# Revit family: Genie_Site_ArticulatingBoom_(SX-180)a
name_source: partatom
category: Site
revit_build: Autodesk Revit 2018 (Build: 20190510_1515(x64)
units: mm (PartAtom-declared; Revit-internal decimal feet)

## family parameters
Always vertical = Yes
Cut with Voids When Loaded = No
OmniClass Number = 23.50.85.17.11
OmniClass Title = Electric and Battery Telescoping Platforms
Part Type = Normal
Round Connector Dimension = Use Diameter
Shared = No
Work Plane-Based = No

## types (1)
- SX-180
    Assembly Code = E1030900
    AssetType = Fixed
    BIMObjectName = Genie_Site_ArticulatingBoom_(SX-180)
    ClassificationName = Uniclass2015
    ClassificationValue = Pr_65_80_47_95
    Color = Grey & Blue
    Cost = 0 $
    Description = The highest reaching model in the line-up, the Genie® SX™-180 telescopic boom lift offers operators access to jobsites inaccessible by other booms, boom trucks and cranes. It is purpose-built to work on jobsites in the oil and gas industries and in industrial or commercial construction and in general maintenance applications.
    DocumentationLiterature = https://www.genielift.com
    DocumentationTechnical = https://www.genielift.com
    DurationUnit = Years
    ExpectedLife = 0
    Features = Genie XChassis™ system extends and retracts to provide stability on the job and a narrow profile for transport. 3.05 m (10 ft) rotating jib with 135˚ vertical and 60˚ horizontal articulation to easily position workers and gear. Standard 2.44 m (8 ft) self-levelling platform with an unrestricted capacity of 340 kg (750 lb). Drive-enable at full height for more productivity on the jobsite. Tackles the most extreme jobs with a working height of 56.9 m (186 ft) and horizontal reach of 24.4 m (80 ft).
    Finish = Painted Steel
    IfcExportAs = IfcTransportElement
    IfcExportType = IfcTransportElementType
    Keynote = X
    Manufacturer = Genie
    ManufacturerName = Genie
    Material = Painted Steel
    Model = Genie - Articulating Boom
    ModelNumber = SX-180
    ModelReference = Genie - Articulating Boom
    NBSDescription = Vertical lifting platforms
    NBSObjectName = Genie - Vertical lifting platforms
    NBSReference = 90-80-65/350
    NominalDepth = 2490 mm
    NominalHeight = 3050 mm  [stored 10.0066 ft]
    NominalLength = 16180 mm
    ProductionYear = 2019
    Size = 2.49m x 3.05m x 16.18m
    Type Comments = SX-180
    TypeName = Genie - Articulating Boom
    URL = http://www.genielift.co.uk
    WarrantyDurationLabor = 0
    WarrantyDurationParts = 0
    WarrantyDurationUnit = Years
    WarrantyGuarantorLabor = http://www.genielift.co.uk
    WarrantyGuarantorParts = http://www.genielift.co.uk
    _BSBibleVersion = 15
    _BimSpecGuid = 0
    _CurrentRevision = 1
    _DistributedBy = www.bimstore.co.uk

note: [stored X ft] marks values corroborated as IEEE doubles in the binary element streams (Revit-internal decimal feet)

## geometry (parser evidence)
native form markers: Sweep x43
no freeform markers — native parametric forms only
